# Revit family: LG_Multi_F_MAX_R32_ODU_U60A_NA_v1.2
name_source: partatom
category: Mechanical Equipment
units: mm (PartAtom-declared; Revit-internal decimal feet)

## family parameters
Always vertical = Yes
Classification = None
Cut with Voids When Loaded = No
Part Type = Normal
Room Calculation Point = No
Round Connector Dimension = Use Diameter
Shared = No
Work Plane-Based = No

## types (3) — shared parameters
Chassis name = U60A
Compressor Motor Output (W) = -
Compressor Type = Scroll
Default Elevation = 0"
Dimensions (WxHxD)(inch) = 37-13/32 x 54-11/32 x 13
Dimensions (WxHxD)(mm) = 950 x 1,380 x 330
Expansion Valve Type = Electronic Expansion Valve
Fan Air Flow Rate (CFM) = 2,295.5 x 2
Fan Air Flow Rate (CMM) = -
Fan Motor Output (W) = 124 x 2
Fan Motor Type = BLDC
Fan Type = Propeller
Pipe Connection_Gas Side (inch) = 3/4
Pipe Connection_Gas Side (mm) = 19.05
Pipe Connection_Liquid Side (inch) = 3/8
Pipe Connection_Liquid Side (mm) = 9.52
Power Supply (Ph_V_Hz) = 1, 208/230 , 60
Power Supply Cable = 8 x 3C
Refrigerant Gas Connection Diameter = 3/4"
Refrigerant Liquid Connection Diameter = 3/8"
Refrigerant Type = R32
Temp Operating Range (Cooling)(C) = -
Temp Operating Range (Cooling)(F) = 14 ~ 118.4
Temp Operating Range (Heating)(C) = -
Temp Operating Range (Heating)(F) = -4.0 ~ 64.4
Type = Multi F MAX R32

## per-type parameters (varying)
| type | Cooling Capacity (Btu/h) | Cooling Capacity (kW) | Heating Capacity (Btu/h) | Heating Capacity (kW) | Model name (Factory) | Net Weight (kg) | Net Weight (lbs) | Power Input (Cooling)(kW) | Power Input (Heating)(kW) | Refrigerant Charge (g) | Running Current (Cooling)(A) | Running Current (Heating)(A) | Sound Power Level Cooling (dB(A)) | Sound Power Level Heating (dB(A)) | Sound Pressure Level Cooling (dB(A)) | Sound Pressure Level Heating (dB(A)) |
| KUMXB481A | 48,000 | 14.10 | 54,000 | 15.80 | Z8UR48GFA0 | 88.0 | 194.0 | 3.75 | 3.81 | (7.5 lbs) | 17.00 | 20.50 | 71 | 72 | 53 | 55 |
| KUMXB541A | 50,500 | 14.80 | 58,000 | 17.00 | Z8UR54GFA0 | 88.0 | 194.0 | 4.01 | 4.04 | (7.5 lbs) | 18.20 | 23.00 | 72 | 73 | 53 | 55 |
| KUMXB601A | 56,000 | 16.40 | 64,000 | 18.80 | Z8UR60GFA0 | 99.0 | 218.3 | 4.67 | 5.46 | (9.26 lbs) | 21.10 | 24.60 | 73 | 74 | 56 | 58 |

note: column(s) folded — value = type name in every type: Model name (Buyer)
